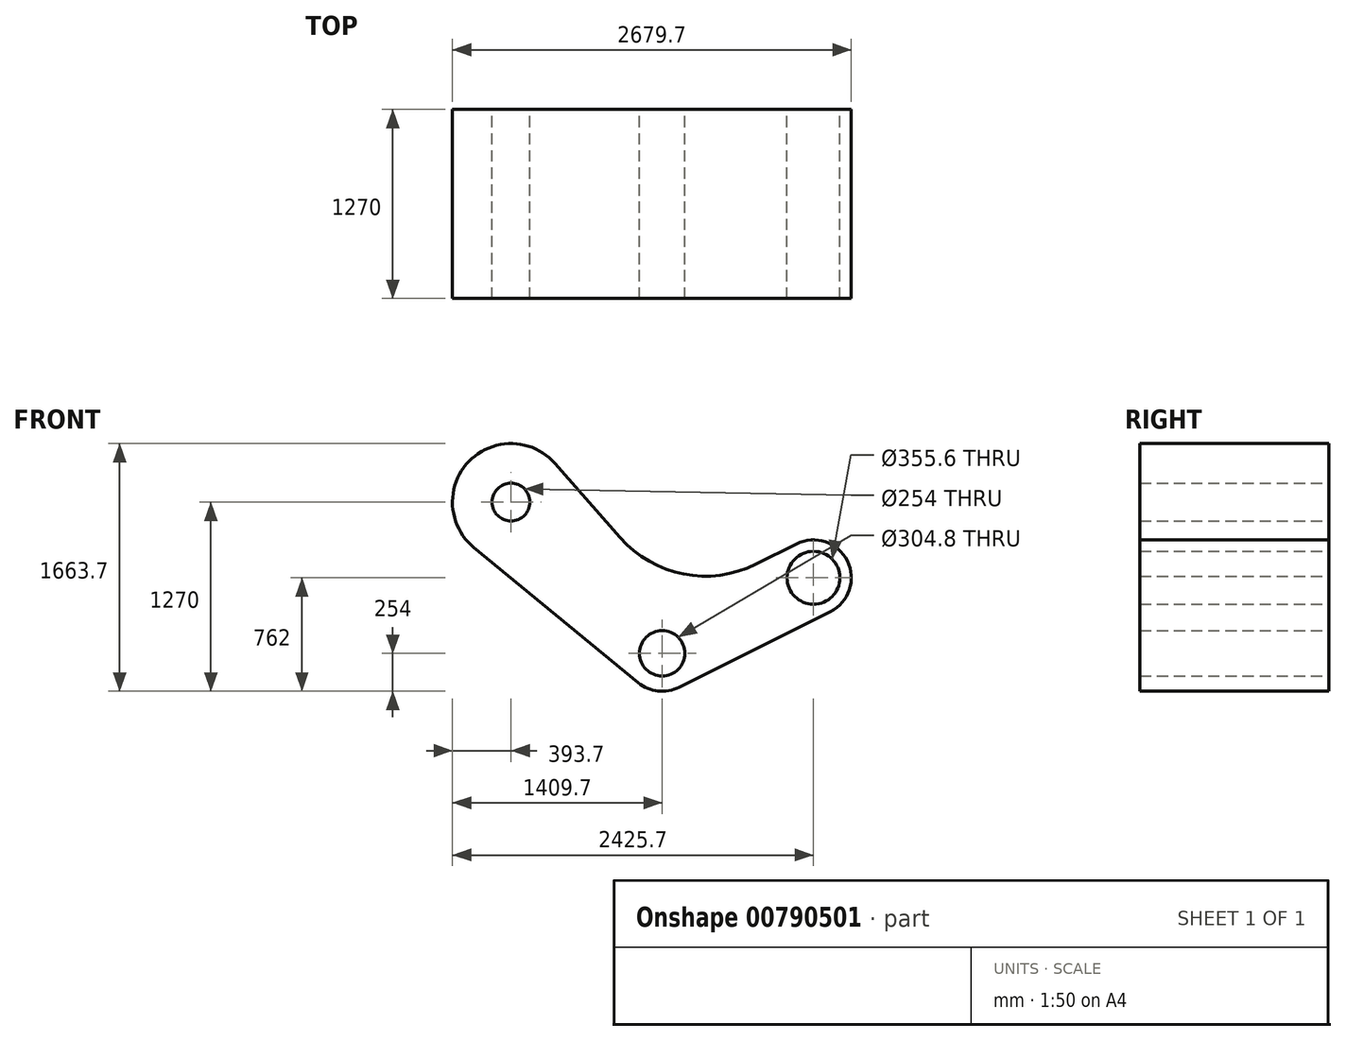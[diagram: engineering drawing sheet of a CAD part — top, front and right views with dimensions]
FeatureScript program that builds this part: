
annotation { "Feature Type Name" : "Feature", "Feature Type Description" : "" }
export const myFeature = defineFeature(function(context is Context, id is Id, definition is map)
    precondition{}
    {
        {
            var Q0;
            Q0=qCreatedBy(makeId("Front.planeOp"),FACE);
            var sketch = newSketch(context, id + "F0", { "sketchPlane" : qUnion([Q0])});
            skCircle(sketch, "E0", {"center": v(0, 0) * mm, "radius": 254 * mm});
            skCircle(sketch, "E1", {"center": v(0, 0) * mm, "radius": 152.4 * mm});
            skCircle(sketch, "E2", {"center": v(-1016, 1016) * mm, "radius": 393.7 * mm});
            skCircle(sketch, "E3", {"center": v(-1016, 1016) * mm, "radius": 127 * mm});
            skCircle(sketch, "E4", {"center": v(1016, 508) * mm, "radius": 254 * mm});
            skCircle(sketch, "E5", {"center": v(1016, 508) * mm, "radius": 177.8 * mm});
            skLineSegment(sketch, "E6", {"start": v(-720.22, 1275.84) * mm, "end": v(-282.76, 777.87) * mm});
            skLineSegment(sketch, "E7", {"start": v(630.49, 599.22) * mm, "end": v(902.4, 735.18) * mm});
            skLineSegment(sketch, "E8", {"start": v(-1266, 711.86) * mm, "end": v(-161.3, -196.22) * mm});
            skLineSegment(sketch, "E9", {"start": v(113.6, -227.18) * mm, "end": v(1129.6, 280.82) * mm});
            skPoint(sketch, "E10.visualSharp", {"position": v(105, 336.48) * mm});
            skArc(sketch, "E10.filletArc", {"start": v(-282.76, 777.87) * mm, "mid": v(143.43, 532.95) * mm, "end": v(630.49, 599.22) * mm});
            skSolve(sketch);
        }
        {
            var Q0;
            Q0=makeQuery(id+"F0.imprint","IMPRINT",FACE,{"disambiguationData":[TD([[makeQuery(id+"F0.imprint","IMPRINT",EDGE,{"derivedFrom":sQuery(id+"F0.wireOp",EDGE,"E3")}),-1.0]])]});
            var Q1;
            {var subQ0=sQuery(id+"F0.wireOp",EDGE,"E6");Q1=makeQuery(id+"F0.imprint","IMPRINT",FACE,{"disambiguationData":[TD([[makeQuery(id+"F0.imprint","IMPRINT",EDGE,{"derivedFrom":subQ0}),-1.0]])]});}
            var Q2;
            Q2=makeQuery(id+"F0.imprint","IMPRINT",FACE,{"disambiguationData":[TD([[makeQuery(id+"F0.imprint","IMPRINT",EDGE,{"derivedFrom":sQuery(id+"F0.wireOp",EDGE,"E1")}),-1.0]])]});
            var Q3;
            Q3=makeQuery(id+"F0.imprint","IMPRINT",FACE,{"disambiguationData":[TD([[makeQuery(id+"F0.imprint","IMPRINT",EDGE,{"derivedFrom":sQuery(id+"F0.wireOp",EDGE,"E5")}),-1.0]])]});
            extrude(context, id + "F1", {"entities" : qUnion([Q0, Q1, Q2, Q3]), "endBound" : BoundingType.SYMMETRIC, "depth" : 1270 * mm, "offsetDistance" : 25.4 * mm});
        }
    });
